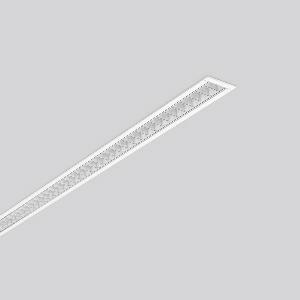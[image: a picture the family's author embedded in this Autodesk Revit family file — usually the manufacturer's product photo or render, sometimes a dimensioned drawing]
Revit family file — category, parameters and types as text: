
# Revit family: less_is_more_27_312179_002_76_239a
name_source: partatom
category: Lighting Fixtures
units: mm (PartAtom-declared; Revit-internal decimal feet)

## family parameters
Cut with Voids When Loaded = No
Host = Face
Light Source = No
Part Type = Normal
Room Calculation Point = No
Round Connector Dimension = Use Diameter
Shared = No

## types (1)
- LESS IS MORE 27 (1 x LED Modul 830, 3500 lm, 3000)
    Apparent Load = 43 VA
    CIE Flux Codes = 90 99 100 100 100
    Color Rendering = 80
    Color Temperature = 3000
    Default Elevation = 1800 mm
    Description = Series: LESS IS MORE 27
Recessed ceiling and wall luminaire with slim design. Housing: extruded aluminium profile, powder-coated. End cap aluminium powder-coated. High polish aluminium micro grid. Perfect for office areas (RUG < 19) and environments with computer screens in accordance with EN 12464-1. Suitable for Recessed ceiling mounting, wall (recessed). External driver with connecting cable. 
Colour: traffic white, matt (RAL 9016)
Length: 1514 mm
Width: 38 mm
Height: 2 mm
Cut-out length: 1506 mm
Cut-out width: 30 mm
Recess height: 45-60 mm
Luminaire: recess height: 37 mm
Lamp: LED
Socket: without socket
Colour temperature: 3000K
Colour rendering index (CRI): 82
System power: 43 W
Rated luminous flux: 3500 lm
Luminous efficiency: 81 lm/W
Control gear: Voltage converter, DALI dim.
Protection class: II
Type of protection: IP 20
    Height = 0 mm  [stored 0 ft]
    Lamp = 1 x LED Modul 830
    Lamp Light Flux = 3500 lm
    Lamp count = 1
    Length = 1514 mm
    Lifetime = 50000 h
    Luminous efficacy = 81 lm/W
    Manufacturer = RZB
    ModVariant = No
    Model = 312179.002.76
    Mounting Place = Ceiling, Wall
    Mounting Type = Recessed
    Number of Poles = 1
    OnlyDefault = Yes
    Power Factor = 1
    Product Name = LESS IS MORE 27
    Product group = Recessed LED linear luminaires
    ProductGroupID = 407
    Protection Class = Protection class II
    Protection Degree = IP 20
    RLX_Detail_Level = 1
    RLX_Emergency_Light_Flux = 0 lm
    RLX_Emergency_Type = 0
    RLX_Emergency_Type_DB = No
    RlxData = <blob elided: 27077 chars, md5=1caea70a>
    Socket = socket
    Standby Power = 0 W
    System Light Flux = 3500 lm
    System Power = 43 W
    Type Comments = Product without accessories
    Type Image = 312177.002.jpg
    URL = http://relux.com
    VarID = ---
    Voltage = 230 V
    Voltage Range = 220-240 V
    Weight = 0.00 kg
    Width = 38 mm

note: [stored X ft] marks values corroborated as IEEE doubles in the binary element streams (Revit-internal decimal feet)

## geometry (parser evidence)
native form markers: Blend x4, Sweep x11
no freeform markers — native parametric forms only
